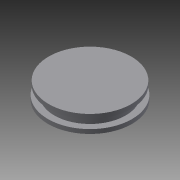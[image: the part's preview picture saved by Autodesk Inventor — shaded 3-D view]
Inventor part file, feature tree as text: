
AUTODESK INVENTOR PART (.ipt)
format: ipt  version: 2015 (Build 190159000, 159)  size: 104,960 bytes
history: native  units: mm
features: sketch x6, extrude x5
ambient origin geometry x8: Origin, YZ Plane, XZ Plane, XY Plane, X Axis, Y Axis, Z Axis, Center Point
bodies: Solid1 (feature_tree)
feature tree (11):
  extrude  "Extrusion1"  Depth=1.0mm TaperAngle=0.0deg
  extrude  "Extrusion2"  Depth=2.0mm TaperAngle=0.0deg
  extrude  "Extrusion3"  Depth=1.0mm
  extrude  "Extrusion4"  Depth=6.5mm
  sketch  "Sketch5"  dims[d11=1.75mm d12=3.25mm]
  extrude  "Extrusion5"  Depth=3.25mm
  sketch  "Sketch1"  dims[d0=20.0mm d1=1.0mm d2=0.0mm]
  sketch  "Sketch2"  dims[d3=17.0mm d4=2.0mm d5=0.0mm]
  sketch  "Sketch3"  dims[d6=1.0mm d7=0.0mm d8=9.0mm]
  sketch  "Sketch4"  dims[d9=3.5mm d10=6.5mm]
  sketch  "Sketch6"  dims[d13=7.0mm d14=0.0mm d15=7.0mm d16=0.0mm]
